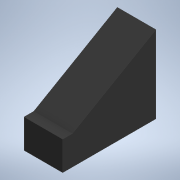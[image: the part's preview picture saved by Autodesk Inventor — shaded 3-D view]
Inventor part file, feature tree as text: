
AUTODESK INVENTOR PART (.ipt)
format: ipt  version: 2020 (Build 240168000, 168)  size: 94,208 bytes
history: native  units: mm
features: extrude x1, sketch x1
ambient origin geometry x8: Origin, YZ Plane, XZ Plane, XY Plane, X Axis, Y Axis, Z Axis, Center Point
bodies: Solid1 (feature_tree)
feature tree (2):
  extrude  "Extrusion1"  TaperAngle=60.0deg  [1 undecoded]
  sketch  "Sketch1"  dims[d0=1000.0mm d1=60.0deg d2=100.0mm d3=300.0mm d4=400.0mm d5=0.0mm]
note: 1 required parameter value undecoded (feature->parameter linkage not recoverable at this tier; creation-order binding heuristic only, values carry confidence <= 0.55)
